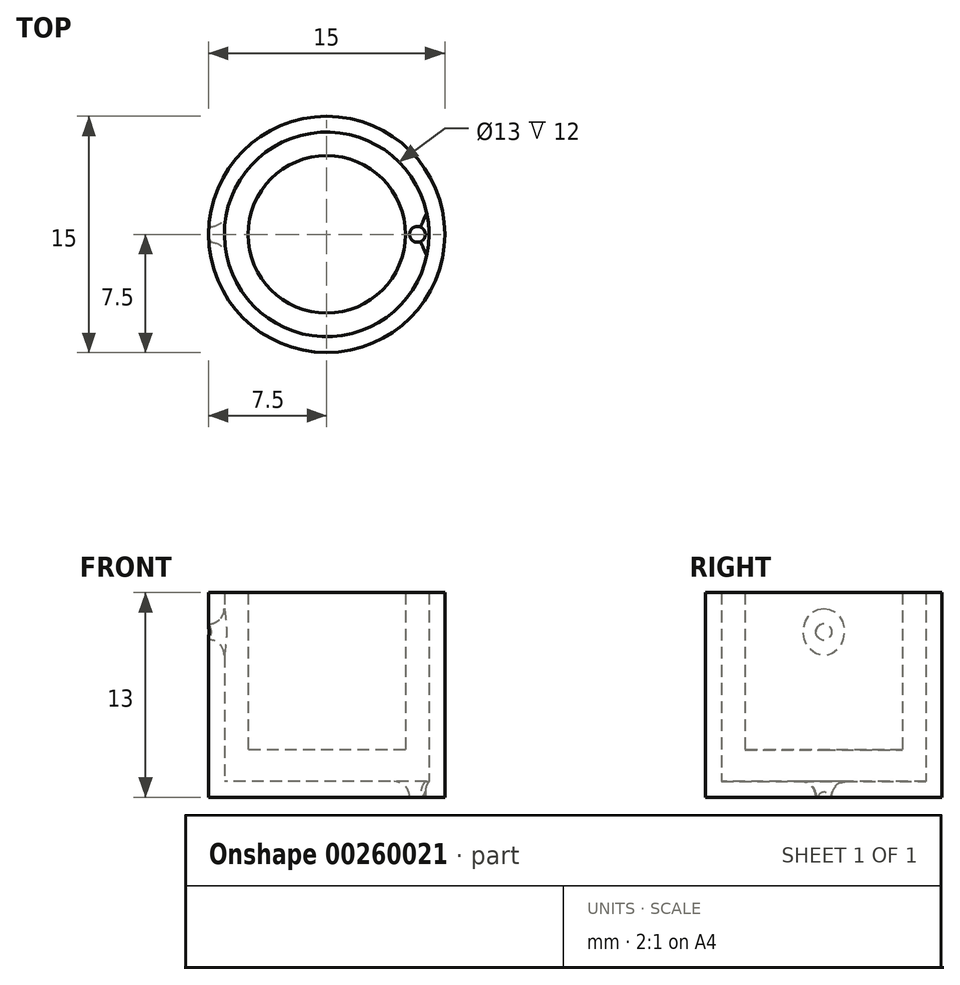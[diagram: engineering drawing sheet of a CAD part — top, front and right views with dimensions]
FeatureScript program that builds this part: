
annotation { "Feature Type Name" : "Feature", "Feature Type Description" : "" }
export const myFeature = defineFeature(function(context is Context, id is Id, definition is map)
    precondition{}
    {
        {
            var Q0;
            Q0=qCreatedBy(makeId("Top.planeOp"),FACE);
            var sketch = newSketch(context, id + "F0", { "sketchPlane" : qUnion([Q0])});
            skCircle(sketch, "E0", {"center": v(0, 0) * mm, "radius": 6.5 * mm});
            skCircle(sketch, "E1.0", {"center": v(0, 0) * mm, "radius": 7.5 * mm});
            skLineSegment(sketch, "E2", {"start": v(0, 0) * mm, "end": v(6.5, 0) * mm});
            skCircle(sketch, "E3", {"center": v(5.77, 0) * mm, "radius": 0.5 * mm});
            skCircle(sketch, "E4", {"center": v(0, 0) * mm, "radius": 5 * mm});
            skSolve(sketch);
        }
        {
            var Q0;
            Q0=makeQuery(id+"F0.imprint","IMPRINT",FACE,{"disambiguationData":[TD([[makeQuery(id+"F0.imprint","IMPRINT",EDGE,{"derivedFrom":sQuery(id+"F0.wireOp",EDGE,"E0")}),-1.0]])]});
            var Q1;
            Q1=makeQuery(id+"F0.imprint","IMPRINT",FACE,{"disambiguationData":[TD([[makeQuery(id+"F0.imprint","IMPRINT",EDGE,{"derivedFrom":sQuery(id+"F0.wireOp",EDGE,"E0")}),1.0]])]});
            var Q2;
            Q2=makeQuery(id+"F0.imprint","IMPRINT",FACE,{"disambiguationData":[TD([[makeQuery(id+"F0.imprint","IMPRINT",EDGE,{"derivedFrom":sQuery(id+"F0.wireOp",EDGE,"E4")}),1.0]])]});
            extrude(context, id + "F1", {"entities" : qUnion([Q0, Q1, Q2]), "depth" : 1 * mm});
        }
        {
            var Q0;
            Q0=makeQuery(id+"F0.imprint","IMPRINT",FACE,{"disambiguationData":[TD([[makeQuery(id+"F0.imprint","IMPRINT",EDGE,{"derivedFrom":sQuery(id+"F0.wireOp",EDGE,"E0")}),-1.0]])]});
            extrude(context, id + "F2", {"entities" : qUnion([Q0]), "operationType" : NewBodyOperationType.ADD, "depth" : 13 * mm});
        }
        {
            var Q0;
            Q0=makeQuery(id+"F1.opExtrude","CAP_EDGE",EDGE,{"disambiguationData":[OSD([sQuery(id+"F0.wireOp",EDGE,"E3")])],"isStart":false});
            fillet(context, id + "F3", {"entities" : qUnion([Q0]), "radius" : 1 * mm, "tangentPropagation" : true, "allowEdgeOverflow" : false});
        }
        {
            var Q0;
            Q0=qCreatedBy(makeId("Right.planeOp"),FACE);
            var sketch = newSketch(context, id + "F4", { "sketchPlane" : qUnion([Q0])});
            skLineSegment(sketch, "E5", {"start": v(0, 0) * mm, "end": v(0, 10.5) * mm});
            skCircle(sketch, "E6", {"center": v(0, 10.5) * mm, "radius": 0.5 * mm});
            skSolve(sketch);
        }
        {
            var Q0;
            Q0=makeQuery(id+"F4.imprint","IMPRINT",FACE,{"disambiguationData":[TD([[makeQuery(id+"F4.imprint","IMPRINT",EDGE,{"derivedFrom":sQuery(id+"F4.wireOp",EDGE,"E6")}),1.0]])]});
            extrude(context, id + "F5", {"entities" : qUnion([Q0]), "operationType" : NewBodyOperationType.REMOVE, "oppositeDirection" : true, "depth" : 25 * mm});
        }
        {
            var Q0;
            Q0=makeQuery(id+"F5.boolean.opBoolean","INTERSECT",EDGE,{"derivedFrom":[makeQuery(id+"F2.opExtrude","SWEPT_FACE",FACE,{"disambiguationData":[OSD([sQuery(id+"F0.wireOp",EDGE,"E0")])]}),makeQuery(id+"F5.opExtrude","SWEPT_FACE",FACE,{"disambiguationData":[OSD([sQuery(id+"F4.wireOp",EDGE,"E6")])]})]});
            fillet(context, id + "F6", {"entities" : qUnion([Q0]), "radius" : 1 * mm, "tangentPropagation" : true, "allowEdgeOverflow" : false});
        }
        {
            var Q0;
            Q0=makeQuery(id+"F0.imprint","IMPRINT",FACE,{"disambiguationData":[TD([[makeQuery(id+"F0.imprint","IMPRINT",EDGE,{"derivedFrom":sQuery(id+"F0.wireOp",EDGE,"E4")}),1.0]])]});
            extrude(context, id + "F7", {"entities" : qUnion([Q0]), "depth" : 10 * mm});
        }
        {
            var Q0;
            Q0=makeQuery(id+"F7.opExtrude","SWEPT_BODY",BODY,{"disambiguationData":[OSD([sQuery(id+"F0.wireOp",EDGE,"E4")])]});
            transform(context, id + "F8", {"entities" : qUnion([Q0]), "transformType" : TransformType.TRANSLATION_3D, "dx" : 0 * mm, "dy" : 0 * mm, "dz" : 3 * mm, "makeCopy" : false});
        }
    });
